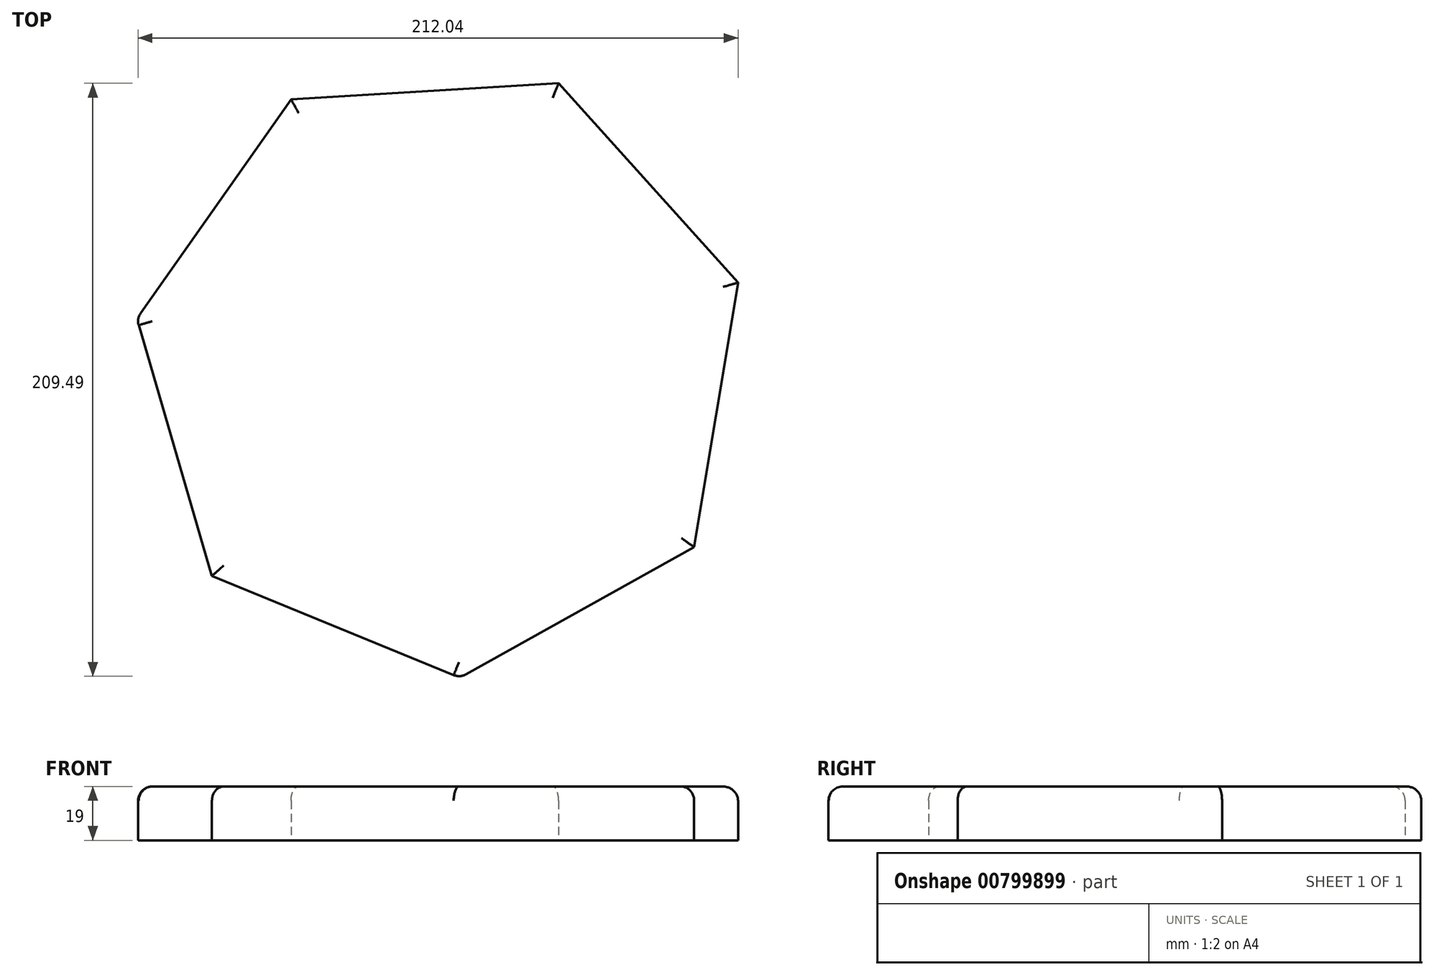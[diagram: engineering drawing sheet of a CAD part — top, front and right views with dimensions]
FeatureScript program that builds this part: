
annotation { "Feature Type Name" : "Feature", "Feature Type Description" : "" }
export const myFeature = defineFeature(function(context is Context, id is Id, definition is map)
    precondition{}
    {
        {
            var Q0;
            Q0=qCreatedBy(makeId("Top.planeOp"),FACE);
            var sketch = newSketch(context, id + "F0", { "sketchPlane" : qUnion([Q0])});
            skCircle(sketch, "E0.cCircle", {"center": v(0, 0) * mm, "radius": 98.38 * mm, "construction": true});
            skLineSegment(sketch, "E0.0", {"start": v(-53.18, 95.36) * mm, "end": v(41.4, 101.04) * mm});
            skLineSegment(sketch, "E0.1", {"start": v(41.4, 101.04) * mm, "end": v(104.8, 30.63) * mm});
            skLineSegment(sketch, "E0.2", {"start": v(104.8, 30.63) * mm, "end": v(89.3, -62.84) * mm});
            skLineSegment(sketch, "E0.3", {"start": v(89.3, -62.84) * mm, "end": v(6.54, -109) * mm});
            skLineSegment(sketch, "E0.4", {"start": v(6.54, -109) * mm, "end": v(-81.13, -73.07) * mm});
            skLineSegment(sketch, "E0.5", {"start": v(-81.13, -73.07) * mm, "end": v(-107.72, 17.88) * mm});
            skLineSegment(sketch, "E0.6", {"start": v(-107.72, 17.88) * mm, "end": v(-53.18, 95.36) * mm});
            skPoint(sketch, "E0.0.midPoint", {"position": v(-5.9, 98.2) * mm});
            skSolve(sketch);
        }
        {
            var Q0;
            Q0 = qSketchRegion(id + "F0", true);
            extrude(context, id + "F1", {"entities" : qUnion([Q0]), "depth" : 19 * mm, "offsetDistance" : 25.4 * mm});
        }
        {
            var Q0;
            Q0=makeQuery(id+"F1.opExtrude","CAP_EDGE",EDGE,{"disambiguationData":[OSD([sQuery(id+"F0.wireOp",EDGE,"E0.5")])],"isStart":false});
            var Q1;
            Q1=makeQuery(id+"F1.opExtrude","CAP_EDGE",EDGE,{"disambiguationData":[OSD([sQuery(id+"F0.wireOp",EDGE,"E0.4")])],"isStart":false});
            fillet(context, id + "F2", {"entities" : qUnion([Q0, Q1]), "radius" : 5 * mm, "tangentPropagation" : true, "allowEdgeOverflow" : false});
        }
        {
            var Q0;
            Q0=makeQuery(id+"F1.opExtrude","CAP_EDGE",EDGE,{"disambiguationData":[OSD([sQuery(id+"F0.wireOp",EDGE,"E0.3")])],"isStart":false});
            var Q1;
            Q1=makeQuery(id+"F1.opExtrude","CAP_EDGE",EDGE,{"disambiguationData":[OSD([sQuery(id+"F0.wireOp",EDGE,"E0.2")])],"isStart":false});
            var Q2;
            Q2=makeQuery(id+"F1.opExtrude","CAP_EDGE",EDGE,{"disambiguationData":[OSD([sQuery(id+"F0.wireOp",EDGE,"E0.1")])],"isStart":false});
            var Q3;
            Q3=makeQuery(id+"F1.opExtrude","CAP_EDGE",EDGE,{"disambiguationData":[OSD([sQuery(id+"F0.wireOp",EDGE,"E0.0")])],"isStart":false});
            var Q4;
            Q4=makeQuery(id+"F1.opExtrude","CAP_EDGE",EDGE,{"disambiguationData":[OSD([sQuery(id+"F0.wireOp",EDGE,"E0.6")])],"isStart":false});
            fillet(context, id + "F3", {"entities" : qUnion([Q0, Q1, Q2, Q3, Q4]), "radius" : 5 * mm, "tangentPropagation" : true, "allowEdgeOverflow" : false});
        }
    });
